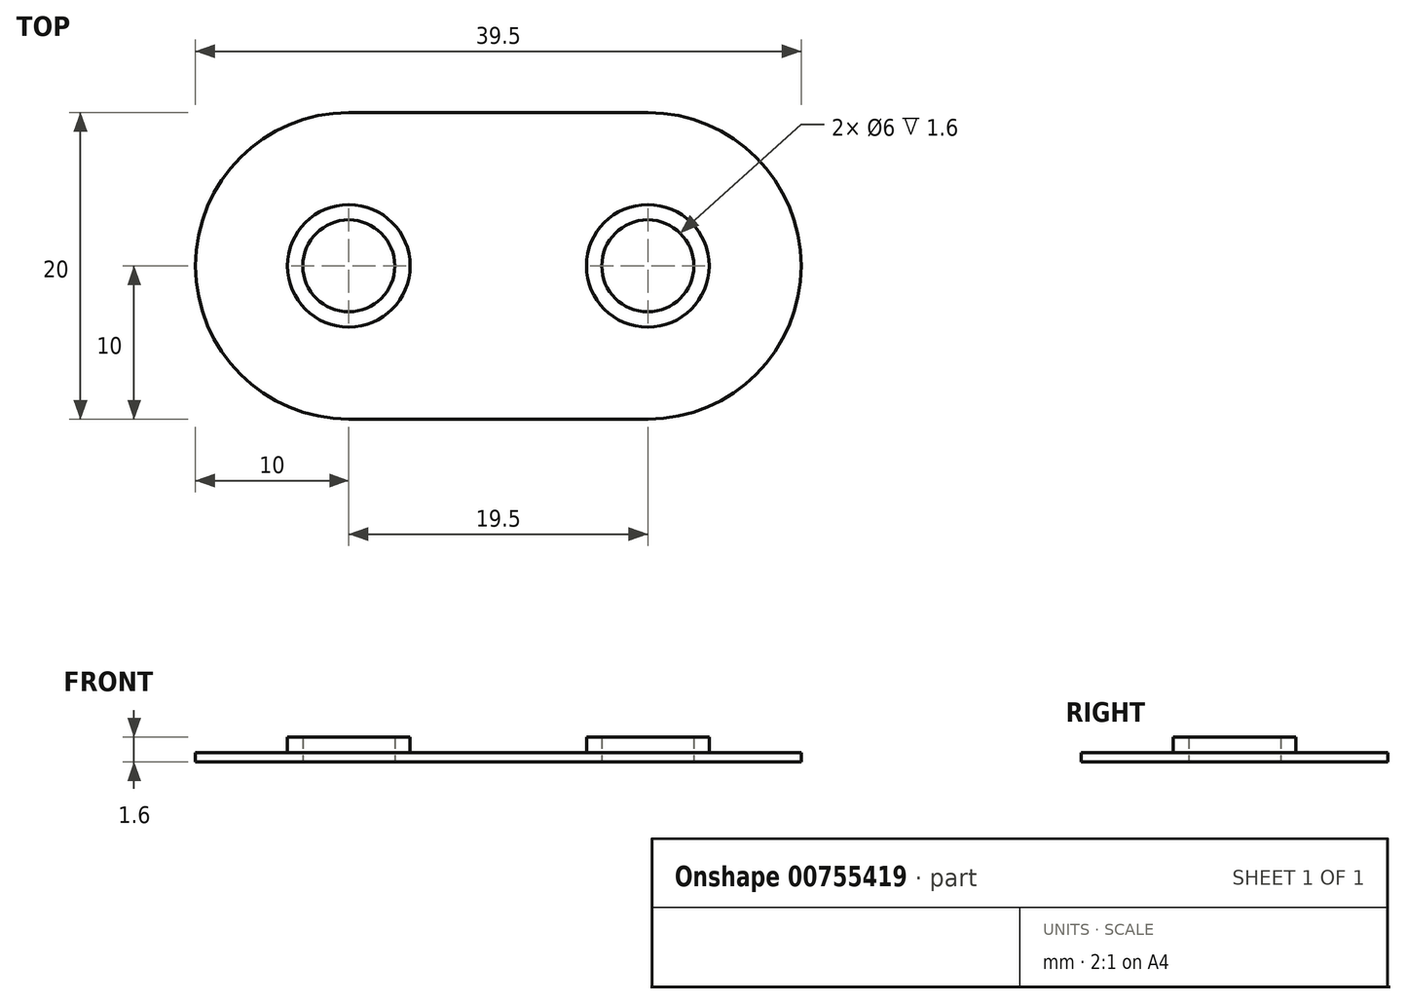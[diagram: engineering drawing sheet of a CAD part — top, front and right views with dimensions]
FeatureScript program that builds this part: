
annotation { "Feature Type Name" : "Feature", "Feature Type Description" : "" }
export const myFeature = defineFeature(function(context is Context, id is Id, definition is map)
    precondition{}
    {
        {
            assignVariable(context, id + "F0", {"name" : "thickness", "anyValue" : .6});
        }
        {
            var Q0;
            Q0=qCreatedBy(makeId("Top.planeOp"),FACE);
            var sketch = newSketch(context, id + "F1", { "sketchPlane" : qUnion([Q0])});
            skCircle(sketch, "E0", {"center": v(0, 0) * mm, "radius": 3 * mm});
            skLineSegment(sketch, "E1", {"start": v(0, 10) * mm, "end": v(19.5, 10) * mm});
            skCircle(sketch, "E2", {"center": v(19.5, 0) * mm, "radius": 3 * mm});
            skArc(sketch, "E3", {"start": v(0, 10) * mm, "mid": v(-10, 0) * mm, "end": v(0, -10) * mm});
            skArc(sketch, "E4", {"start": v(19.5, -10) * mm, "mid": v(29.5, 0) * mm, "end": v(19.5, 10) * mm});
            skLineSegment(sketch, "E5", {"start": v(0, -10) * mm, "end": v(19.5, -10) * mm});
            skSolve(sketch);
        }
        {
            var Q0;
            Q0 = qSketchRegion(id + "F1", true);
            extrude(context, id + "F2", {"entities" : qUnion([Q0]), "depth" : (getVariable(context, 'thickness')) * mm, "offsetDistance" : 25 * mm});
        }
        {
            var Q0;
            Q0=makeQuery(id+"F2.opExtrude","CAP_FACE",FACE,{"disambiguationData":[OSD([sQuery(id+"F1.wireOp",EDGE,"E0"),sQuery(id+"F1.wireOp",EDGE,"E1"),sQuery(id+"F1.wireOp",EDGE,"E2"),sQuery(id+"F1.wireOp",EDGE,"E3"),sQuery(id+"F1.wireOp",EDGE,"E4"),sQuery(id+"F1.wireOp",EDGE,"E5")])],"isStart":false});
            var sketch = newSketch(context, id + "F3", { "sketchPlane" : qUnion([Q0])});
            skCircle(sketch, "E6", {"center": v(0, 0) * mm, "radius": 4 * mm});
            skCircle(sketch, "E7", {"center": v(19.5, 0) * mm, "radius": 4 * mm});
            skCircle(sketch, "E8.0", {"center": v(0, 0) * mm, "radius": 3 * mm});
            skCircle(sketch, "E9.0", {"center": v(19.5, 0) * mm, "radius": 3 * mm});
            skSolve(sketch);
        }
        {
            var Q0;
            Q0 = qSketchRegion(id + "F3", true);
            extrude(context, id + "F4", {"entities" : qUnion([Q0]), "operationType" : NewBodyOperationType.ADD, "depth" : 1 * mm, "offsetDistance" : 25 * mm});
        }
    });
